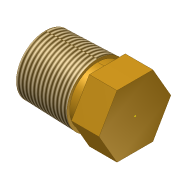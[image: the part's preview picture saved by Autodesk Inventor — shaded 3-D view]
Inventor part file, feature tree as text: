
AUTODESK INVENTOR PART (.ipt)
format: ipt  version: Autodesk Inventor 10  size: 174,080 bytes
history: native  units: mm (DEFAULTED — no unit token found)
features: thread x2, sketch x1, imported_body x1
ambient origin geometry x8: Origin, YZ Plane, XZ Plane, XY Plane, X Axis, Y Axis, Z Axis, Center Point
feature tree (4):
  sketch  "Sketch1"
  imported_body  "Base1"
  thread  "Thread1"  [1 undecoded]
  thread  "Thread2"  [1 undecoded]
note: 2 required parameter values undecoded (feature->parameter linkage not recoverable at this tier; creation-order binding heuristic only, values carry confidence <= 0.55)
